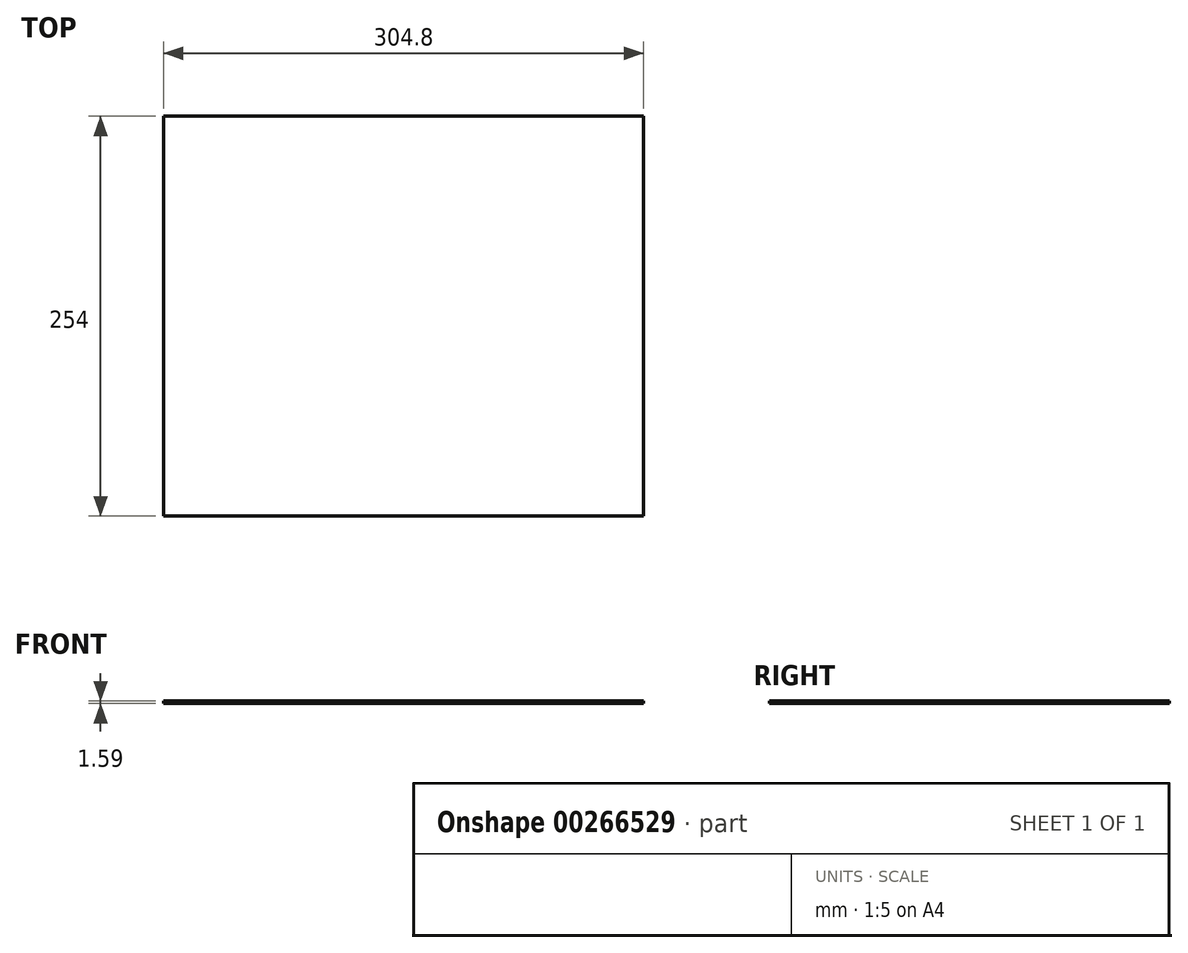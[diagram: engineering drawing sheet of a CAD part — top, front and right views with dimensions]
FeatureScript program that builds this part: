
annotation { "Feature Type Name" : "Feature", "Feature Type Description" : "" }
export const myFeature = defineFeature(function(context is Context, id is Id, definition is map)
    precondition{}
    {
        {
            var Q0;
            Q0=qCreatedBy(makeId("Top.planeOp"),FACE);
            var sketch = newSketch(context, id + "F0", { "sketchPlane" : qUnion([Q0])});
            skLineSegment(sketch, "E0.bottom", {"start": v(0, 0) * mm, "end": v(304.8, 0) * mm});
            skLineSegment(sketch, "E0.top", {"start": v(0, 254) * mm, "end": v(304.8, 254) * mm});
            skLineSegment(sketch, "E0.left", {"start": v(0, 0) * mm, "end": v(0, 254) * mm});
            skLineSegment(sketch, "E0.right", {"start": v(304.8, 0) * mm, "end": v(304.8, 254) * mm});
            skSolve(sketch);
        }
        {
            var Q0;
            Q0=makeQuery(id+"F0.imprint","IMPRINT",FACE,{"disambiguationData":[TD([[makeQuery(id+"F0.imprint","IMPRINT",EDGE,{"derivedFrom":sQuery(id+"F0.wireOp",EDGE,"E0.bottom")}),1.0]])]});
            extrude(context, id + "F1", {"entities" : qUnion([Q0]), "depth" : 1.59 * mm});
        }
    });
